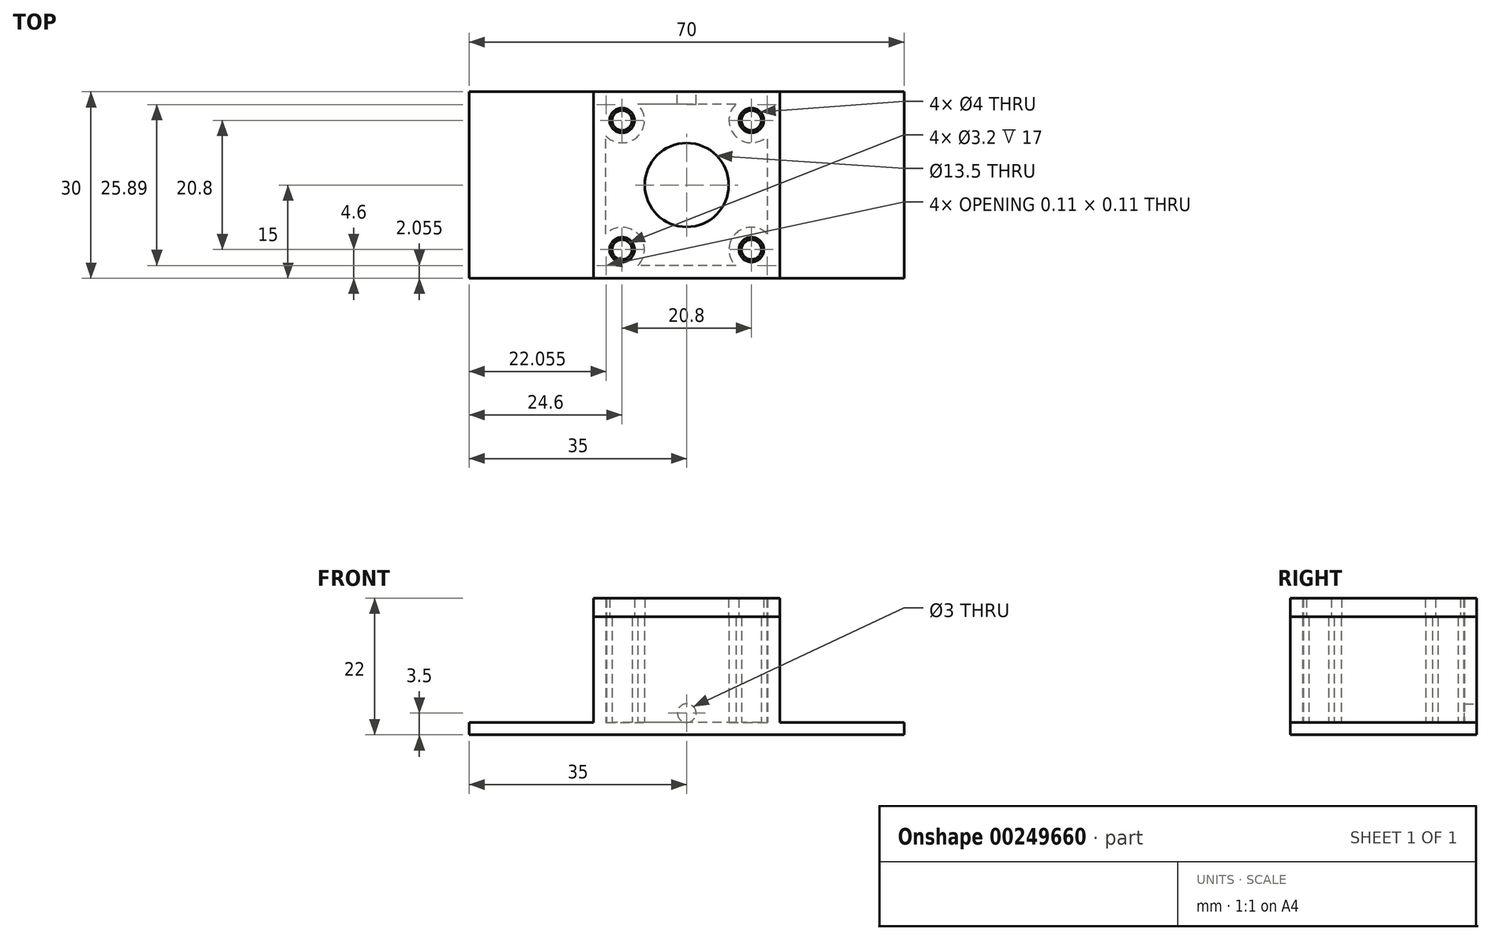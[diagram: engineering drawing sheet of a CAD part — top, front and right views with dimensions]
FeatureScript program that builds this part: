
annotation { "Feature Type Name" : "Feature", "Feature Type Description" : "" }
export const myFeature = defineFeature(function(context is Context, id is Id, definition is map)
    precondition{}
    {
        {
            var Q0;
            Q0=qCreatedBy(makeId("Top.planeOp"),FACE);
            var sketch = newSketch(context, id + "F0", { "sketchPlane" : qUnion([Q0])});
            skLineSegment(sketch, "E0.bottom", {"start": v(35, -15) * mm, "end": v(-35, -15) * mm});
            skLineSegment(sketch, "E0.top", {"start": v(35, 15) * mm, "end": v(-35, 15) * mm});
            skLineSegment(sketch, "E0.left", {"start": v(35, -15) * mm, "end": v(35, 15) * mm});
            skLineSegment(sketch, "E0.right", {"start": v(-35, -15) * mm, "end": v(-35, 15) * mm});
            skPoint(sketch, "E0.middle", {"position": v(0, 0) * mm});
            skSolve(sketch);
        }
        {
            var Q0;
            Q0=makeQuery(id+"F0.imprint","IMPRINT",FACE,{"disambiguationData":[TD([[makeQuery(id+"F0.imprint","IMPRINT",EDGE,{"derivedFrom":sQuery(id+"F0.wireOp",EDGE,"E0.bottom")}),-1.0]])]});
            extrude(context, id + "F1", {"entities" : qUnion([Q0]), "oppositeDirection" : true, "depth" : 2 * mm});
        }
        {
            var Q0;
            Q0=makeQuery(id+"F1.opExtrude","CAP_FACE",FACE,{"disambiguationData":[OSD([sQuery(id+"F0.wireOp",EDGE,"E0.bottom"),sQuery(id+"F0.wireOp",EDGE,"E0.top"),sQuery(id+"F0.wireOp",EDGE,"E0.left"),sQuery(id+"F0.wireOp",EDGE,"E0.right")])],"isStart":true});
            var sketch = newSketch(context, id + "F2", { "sketchPlane" : qUnion([Q0])});
            skLineSegment(sketch, "E1.bottom", {"start": v(-15, 15) * mm, "end": v(15, 15) * mm});
            skLineSegment(sketch, "E1.top", {"start": v(-15, -15) * mm, "end": v(15, -15) * mm});
            skLineSegment(sketch, "E1.left", {"start": v(-15, 15) * mm, "end": v(-15, -15) * mm});
            skLineSegment(sketch, "E1.right", {"start": v(15, 15) * mm, "end": v(15, -15) * mm});
            skLineSegment(sketch, "E2.bottom", {"start": v(13, -13) * mm, "end": v(12.89, -13) * mm});
            skLineSegment(sketch, "E2.top", {"start": v(13, 13) * mm, "end": v(12.89, 13) * mm});
            skLineSegment(sketch, "E2.left", {"start": v(13, -13) * mm, "end": v(13, -12.89) * mm});
            skLineSegment(sketch, "E2.right", {"start": v(-13, -13) * mm, "end": v(-13, -12.89) * mm});
            skPoint(sketch, "E2.middle", {"position": v(0, 0) * mm});
            skCircle(sketch, "E3", {"center": v(-10.4, 10.4) * mm, "radius": 1.6 * mm});
            skArc(sketch, "E4", {"start": v(-12.89, 13) * mm, "mid": v(-12.95, 12.95) * mm, "end": v(-13, 12.89) * mm});
            skArc(sketch, "E5.trimOffspring", {"start": v(-13, 7.91) * mm, "mid": v(-7.85, 7.85) * mm, "end": v(-7.91, 13) * mm});
            skLineSegment(sketch, "E6.trimOffspring", {"start": v(-12.89, 13) * mm, "end": v(-13, 13) * mm});
            skLineSegment(sketch, "E7.trimOffspring", {"start": v(-13, 12.89) * mm, "end": v(-13, 13) * mm});
            skCircle(sketch, "E8", {"center": v(-10.4, -10.4) * mm, "radius": 1.6 * mm});
            skArc(sketch, "E9", {"start": v(-13, -12.89) * mm, "mid": v(-12.95, -12.95) * mm, "end": v(-12.89, -13) * mm});
            skLineSegment(sketch, "E10.trimOffspring", {"start": v(-13, -7.91) * mm, "end": v(-13, 7.91) * mm});
            skArc(sketch, "E11.trimOffspring", {"start": v(-7.91, -13) * mm, "mid": v(-7.85, -7.85) * mm, "end": v(-13, -7.91) * mm});
            skLineSegment(sketch, "E12.trimOffspring", {"start": v(-12.89, -13) * mm, "end": v(-13, -13) * mm});
            skCircle(sketch, "E13", {"center": v(10.4, -10.4) * mm, "radius": 1.6 * mm});
            skArc(sketch, "E14", {"start": v(12.89, -13) * mm, "mid": v(12.95, -12.95) * mm, "end": v(13, -12.89) * mm});
            skLineSegment(sketch, "E15.trimOffspring", {"start": v(7.91, -13) * mm, "end": v(-7.91, -13) * mm});
            skArc(sketch, "E16.trimOffspring", {"start": v(13, -7.91) * mm, "mid": v(7.85, -7.85) * mm, "end": v(7.91, -13) * mm});
            skLineSegment(sketch, "E17.trimOffspring", {"start": v(13, -7.91) * mm, "end": v(13, 7.91) * mm});
            skCircle(sketch, "E18", {"center": v(10.4, 10.4) * mm, "radius": 1.6 * mm});
            skArc(sketch, "E19", {"start": v(7.91, 13) * mm, "mid": v(7.85, 7.85) * mm, "end": v(13, 7.91) * mm});
            skLineSegment(sketch, "E20.trimOffspring", {"start": v(7.91, 13) * mm, "end": v(-7.91, 13) * mm});
            skArc(sketch, "E21.trimOffspring", {"start": v(13, 12.89) * mm, "mid": v(12.95, 12.95) * mm, "end": v(12.89, 13) * mm});
            skLineSegment(sketch, "E22.trimOffspring", {"start": v(13, 12.89) * mm, "end": v(13, 13) * mm});
            skSolve(sketch);
        }
        {
            var Q0;
            Q0=makeQuery(id+"F2.imprint","IMPRINT",FACE,{"disambiguationData":[TD([[makeQuery(id+"F2.imprint","IMPRINT",EDGE,{"derivedFrom":sQuery(id+"F2.wireOp",EDGE,"E1.bottom")}),1.0]])]});
            extrude(context, id + "F3", {"entities" : qUnion([Q0]), "operationType" : NewBodyOperationType.ADD, "depth" : 17 * mm});
        }
        {
            var Q0;
            Q0=makeQuery(id+"F3.opExtrude","CAP_FACE",FACE,{"disambiguationData":[OSD([sQuery(id+"F2.wireOp",EDGE,"E1.bottom"),sQuery(id+"F2.wireOp",EDGE,"E1.top"),sQuery(id+"F2.wireOp",EDGE,"E1.left"),sQuery(id+"F2.wireOp",EDGE,"E1.right"),sQuery(id+"F2.wireOp",EDGE,"E2.bottom"),sQuery(id+"F2.wireOp",EDGE,"E2.top"),sQuery(id+"F2.wireOp",EDGE,"E2.left"),sQuery(id+"F2.wireOp",EDGE,"E2.right"),sQuery(id+"F2.wireOp",EDGE,"E3"),sQuery(id+"F2.wireOp",EDGE,"E4"),sQuery(id+"F2.wireOp",EDGE,"E5.trimOffspring"),sQuery(id+"F2.wireOp",EDGE,"E6.trimOffspring"),sQuery(id+"F2.wireOp",EDGE,"E7.trimOffspring"),sQuery(id+"F2.wireOp",EDGE,"E8"),sQuery(id+"F2.wireOp",EDGE,"E9"),sQuery(id+"F2.wireOp",EDGE,"E10.trimOffspring"),sQuery(id+"F2.wireOp",EDGE,"E11.trimOffspring"),sQuery(id+"F2.wireOp",EDGE,"E12.trimOffspring"),sQuery(id+"F2.wireOp",EDGE,"E13"),sQuery(id+"F2.wireOp",EDGE,"E14"),sQuery(id+"F2.wireOp",EDGE,"E15.trimOffspring"),sQuery(id+"F2.wireOp",EDGE,"E16.trimOffspring"),sQuery(id+"F2.wireOp",EDGE,"E17.trimOffspring"),sQuery(id+"F2.wireOp",EDGE,"E18"),sQuery(id+"F2.wireOp",EDGE,"E19"),sQuery(id+"F2.wireOp",EDGE,"E20.trimOffspring"),sQuery(id+"F2.wireOp",EDGE,"E21.trimOffspring"),sQuery(id+"F2.wireOp",EDGE,"E22.trimOffspring")])],"isStart":false});
            var sketch = newSketch(context, id + "F4", { "sketchPlane" : qUnion([Q0])});
            skLineSegment(sketch, "E23.bottom", {"start": v(15, -15) * mm, "end": v(-15, -15) * mm});
            skLineSegment(sketch, "E23.top", {"start": v(15, 15) * mm, "end": v(-15, 15) * mm});
            skLineSegment(sketch, "E23.left", {"start": v(15, -15) * mm, "end": v(15, 15) * mm});
            skLineSegment(sketch, "E23.right", {"start": v(-15, -15) * mm, "end": v(-15, 15) * mm});
            skPoint(sketch, "E23.middle", {"position": v(0, 0) * mm});
            skCircle(sketch, "E24", {"center": v(-10.4, 10.4) * mm, "radius": 2 * mm});
            skCircle(sketch, "E25", {"center": v(10.4, 10.4) * mm, "radius": 2 * mm});
            skCircle(sketch, "E26", {"center": v(10.4, -10.4) * mm, "radius": 2 * mm});
            skCircle(sketch, "E27", {"center": v(-10.4, -10.4) * mm, "radius": 2 * mm});
            skCircle(sketch, "E28", {"center": v(0, 0) * mm, "radius": 6.75 * mm});
            skSolve(sketch);
        }
        {
            var Q0;
            Q0=makeQuery(id+"F4.imprint","IMPRINT",FACE,{"disambiguationData":[TD([[makeQuery(id+"F4.imprint","IMPRINT",EDGE,{"derivedFrom":sQuery(id+"F4.wireOp",EDGE,"E23.bottom")}),-1.0]])]});
            var Q1;
            Q1=makeQuery(id+"F4.imprint","IMPRINT",FACE,{"disambiguationData":[TD([[makeQuery(id+"F4.imprint","IMPRINT",EDGE,{"derivedFrom":sQuery(id+"F4.wireOp",EDGE,"E28")}),-1.0]])]});
            extrude(context, id + "F5", {"entities" : qUnion([Q0, Q1]), "depth" : 3 * mm});
        }
        {
            var Q0;
            Q0=makeQuery(id+"F3.boolean.opBoolean","MERGE",FACE,{"derivedFrom":[makeQuery(id+"F1.opExtrude","SWEPT_FACE",FACE,{"disambiguationData":[OSD([sQuery(id+"F0.wireOp",EDGE,"E0.top")])]}),makeQuery(id+"F3.opExtrude","SWEPT_FACE",FACE,{"disambiguationData":[OSD([sQuery(id+"F2.wireOp",EDGE,"E1.bottom")])]})]});
            var sketch = newSketch(context, id + "F6", { "sketchPlane" : qUnion([Q0])});
            skCircle(sketch, "E29", {"center": v(0, 1.5) * mm, "radius": 1.5 * mm});
            skSolve(sketch);
        }
        {
            var Q0;
            Q0=makeQuery(id+"F6.imprint","IMPRINT",FACE,{"disambiguationData":[TD([[makeQuery(id+"F6.imprint","IMPRINT",EDGE,{"derivedFrom":sQuery(id+"F6.wireOp",EDGE,"E29")}),1.0]])]});
            var Q1;
            Q1=makeQuery(id+"F3.opExtrude","SWEPT_FACE",FACE,{"disambiguationData":[OSD([sQuery(id+"F2.wireOp",EDGE,"E20.trimOffspring")])]});
            extrude(context, id + "F7", {"entities" : qUnion([Q0]), "operationType" : NewBodyOperationType.REMOVE, "endBound" : BoundingType.UP_TO_SURFACE, "oppositeDirection" : true, "endBoundEntityFace" : qUnion([Q1]), "depth" : 25 * mm});
        }
    });
